# Revit family: PRESTO 1000 A Cromo Brillo
name_source: partatom
category: Aparatos sanitarios
revit_build: Autodesk Revit 2015 (Build: 20140223_1515(x64)
units: mm (PartAtom-declared; Revit-internal decimal feet)

## types (1)
- 19500
    Accionamiento = Por pulsador
    CAUDAL = 1.2 L/Min
    CIERRE = Automátiaco a los 7 seg
    Comentarios de tipo = ◦Suministrado con arandela, tuerca racor de salida y junta americana para tubo de Ø 28 mm
◦Dispositivo antiSifónico incorporado
◦Presión dinámica mínima que necesita a la entrada el fluxor: 0,900 bar
◦Pistón intercambiable que comprende todo el mecanismo del fluxor
◦Apertura por pulsador
◦Caja de empotrar y placa de fijación intermedia fabricadas con protección antioxidante
◦Pulsador y tapa en ABS pintado o cromado
◦Cuerpo del fluxor en latón niquelado con piezas interiores en materiales resistentes a la corrosión y a las incrustaciones calcáreas.
    Conexión AC = Sí
    Conexión AF = Sí
    Código de montaje = C1030220
    Descripción = Fluxor temporizado para encastrar con cuerpo de latón y caja de empotrar con protección antioxidante. Dispositivo antiSifónico incorporado. Pistón intercambiable.
    ENTRADA = Macho 1"
    Elevación por defecto = 1219 mm
    Fabricante = PRESTO IBÉRICA
    Imagen de tipo = <Ninguno>
    Material = Presto Ibérica: CROMO BRILLO
    Modelo = PRESTO 1000 A
    PESO BRUTO = 1.550 Kg
    REFERENCIA = 19500
    Teléfono = (+34) 915 782 575
    URL = http://www.prestoiberica.com

## geometry (parser evidence)
native form markers: Blend x3
no freeform markers — native parametric forms only
